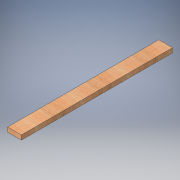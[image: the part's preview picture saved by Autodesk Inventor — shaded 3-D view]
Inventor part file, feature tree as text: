
AUTODESK INVENTOR PART (.ipt)
format: ipt  version: 2016 (Build 200138000, 138)  size: 113,152 bytes
history: native  units: in
note: dims shown in document units (in); Inventor stores cm internally (conversion verified against a paired STEP export)
features: extrude x1, sketch x1
ambient origin geometry x8: Origin, YZ Plane, XZ Plane, XY Plane, X Axis, Y Axis, Z Axis, Center Point
bodies: Solid1 (feature_tree)
feature tree (2):
  extrude  "Extrusion1"  Depth=33.0in
  sketch  "Sketch1"  dims[d0=3.0in d1=33.0in d2=1.0in d3=0.0in]
